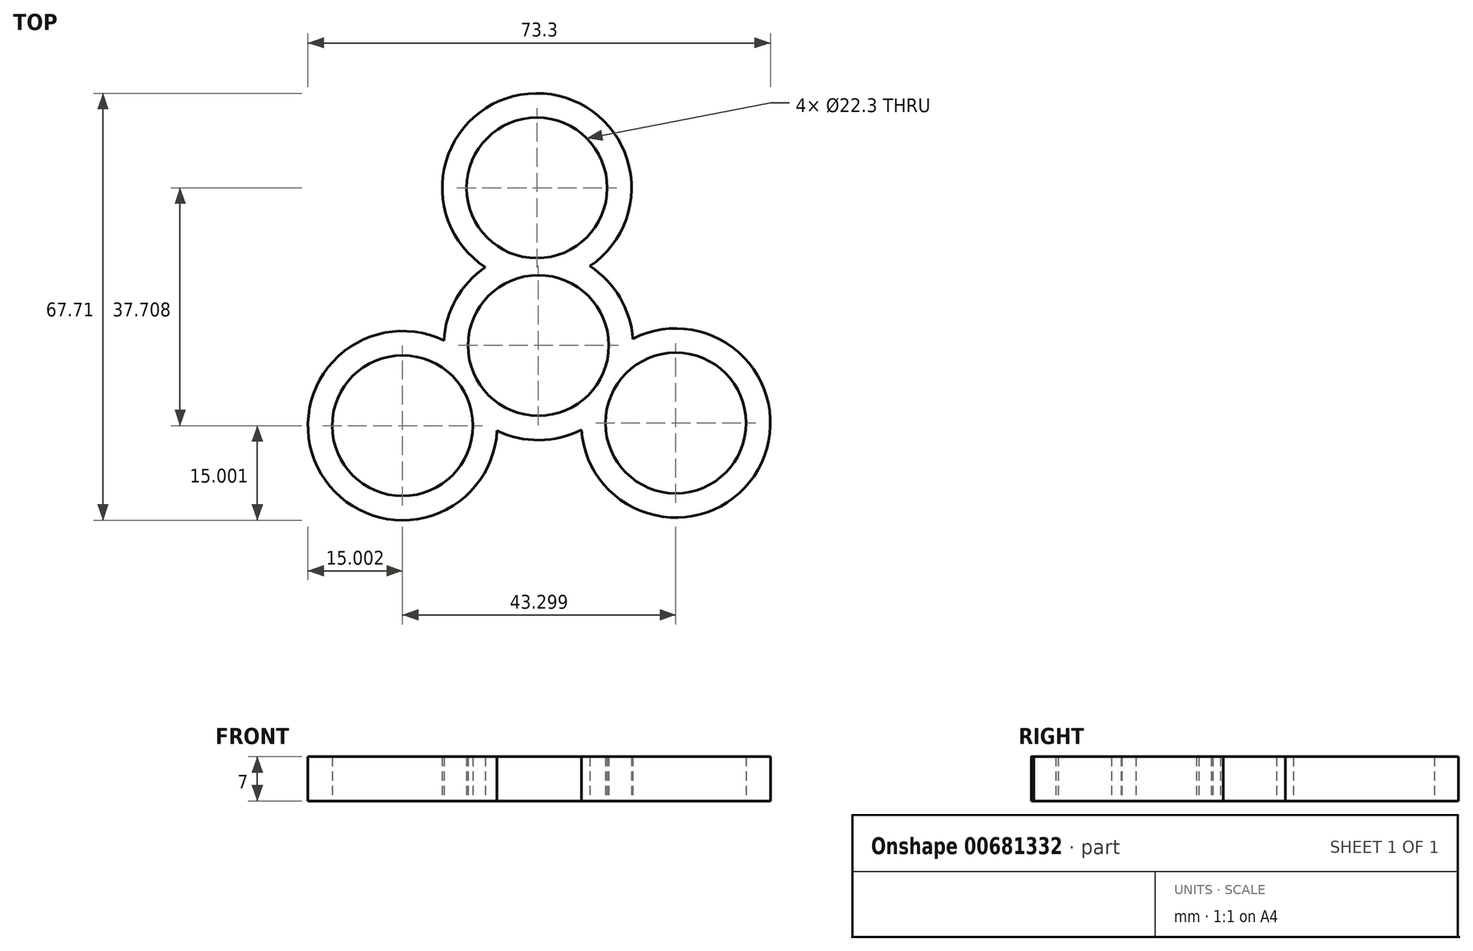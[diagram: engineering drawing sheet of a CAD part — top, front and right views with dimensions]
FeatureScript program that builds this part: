
annotation { "Feature Type Name" : "Feature", "Feature Type Description" : "" }
export const myFeature = defineFeature(function(context is Context, id is Id, definition is map)
    precondition{}
    {
        {
            var Q0;
            Q0=qCreatedBy(makeId("Top.planeOp"),FACE);
            var sketch = newSketch(context, id + "F0", { "sketchPlane" : qUnion([Q0])});
            skPoint(sketch, "E0.0.midPoint", {"position": v(22.1, 13.05) * mm});
            skLineSegment(sketch, "E1", {"start": v(0, 0) * mm, "end": v(-0.49, 50) * mm});
            skLineSegment(sketch, "E2", {"start": v(0, 0) * mm, "end": v(43.54, -24.58) * mm});
            skLineSegment(sketch, "E3", {"start": v(0, 0) * mm, "end": v(-43.06, -25.42) * mm});
            skCircle(sketch, "E4", {"center": v(-21.53, -12.7) * mm, "radius": 11.15 * mm});
            skCircle(sketch, "E5", {"center": v(21.77, -12.29) * mm, "radius": 11.15 * mm});
            skCircle(sketch, "E6", {"center": v(-0.24, 25) * mm, "radius": 11.15 * mm});
            skCircle(sketch, "E7", {"center": v(0, 0) * mm, "radius": 11.15 * mm});
            skPoint(sketch, "E8", {"position": v(31.48, -17.77) * mm});
            skCircle(sketch, "E9", {"center": v(-0.24, 25) * mm, "radius": 15 * mm});
            skCircle(sketch, "E10", {"center": v(21.77, -12.29) * mm, "radius": 15 * mm});
            skCircle(sketch, "E11", {"center": v(-21.53, -12.7) * mm, "radius": 15 * mm});
            skCircle(sketch, "E12", {"center": v(0, 0) * mm, "radius": 15 * mm});
            skSolve(sketch);
        }
        {
            var Q0;
            {var subQ3=sQuery(id+"F0.wireOp",EDGE,"E1");var subQ5=sQuery(id+"F0.wireOp",EDGE,"E7");var subQ11=makeQuery(id+"F0.imprint","INTERSECT",VERTEX,{"derivedFrom":[subQ3,subQ5]});Q0=makeQuery(id+"F0.imprint","IMPRINT",FACE,{"disambiguationData":[TD([[makeQuery(id+"F0.imprint","IMPRINT",EDGE,{"disambiguationData":[TD([[subQ11,-1.0]])],"derivedFrom":subQ3}),-1.0]])]});}
            var Q1;
            {var subQ3=sQuery(id+"F0.wireOp",EDGE,"E2");var subQ9=sQuery(id+"F0.wireOp",EDGE,"E7");var subQ11=makeQuery(id+"F0.imprint","INTERSECT",VERTEX,{"derivedFrom":[subQ3,subQ9]});Q1=makeQuery(id+"F0.imprint","IMPRINT",FACE,{"disambiguationData":[TD([[makeQuery(id+"F0.imprint","IMPRINT",EDGE,{"disambiguationData":[TD([[subQ11,-1.0]])],"derivedFrom":subQ3}),-1.0]])]});}
            var Q2;
            {var subQ5=sQuery(id+"F0.wireOp",EDGE,"E7");var subQ6=sQuery(id+"F0.wireOp",EDGE,"E1");var subQ7=makeQuery(id+"F0.imprint","INTERSECT",VERTEX,{"derivedFrom":[subQ6,subQ5]});Q2=makeQuery(id+"F0.imprint","IMPRINT",FACE,{"disambiguationData":[TD([[makeQuery(id+"F0.imprint","IMPRINT",EDGE,{"disambiguationData":[TD([[subQ7,-1.0]])],"derivedFrom":subQ6}),1.0]])]});}
            var Q3;
            {var subQ0=sQuery(id+"F0.wireOp",EDGE,"E9");var subQ1=sQuery(id+"F0.wireOp",EDGE,"E7");var subQ2=makeQuery(id+"F0.imprint","INTERSECT",VERTEX,{"disambiguationData":[OD(1.0)],"derivedFrom":[subQ1,subQ0]});Q3=makeQuery(id+"F0.imprint","IMPRINT",FACE,{"disambiguationData":[TD([[makeQuery(id+"F0.imprint","IMPRINT",EDGE,{"disambiguationData":[TD([[subQ2,-1.0]])],"derivedFrom":subQ1}),-1.0]])]});}
            var Q4;
            {var subQ0=sQuery(id+"F0.wireOp",EDGE,"E9");var subQ1=sQuery(id+"F0.wireOp",EDGE,"E7");var subQ2=makeQuery(id+"F0.imprint","INTERSECT",VERTEX,{"disambiguationData":[OD(0.0)],"derivedFrom":[subQ1,subQ0]});Q4=makeQuery(id+"F0.imprint","IMPRINT",FACE,{"disambiguationData":[TD([[makeQuery(id+"F0.imprint","IMPRINT",EDGE,{"disambiguationData":[TD([[subQ2,1.0]])],"derivedFrom":subQ1}),-1.0]])]});}
            var Q5;
            {var subQ0=sQuery(id+"F0.wireOp",EDGE,"E11");var subQ1=sQuery(id+"F0.wireOp",EDGE,"E7");var subQ2=makeQuery(id+"F0.imprint","INTERSECT",VERTEX,{"disambiguationData":[OD(1.0)],"derivedFrom":[subQ1,subQ0]});Q5=makeQuery(id+"F0.imprint","IMPRINT",FACE,{"disambiguationData":[TD([[makeQuery(id+"F0.imprint","IMPRINT",EDGE,{"disambiguationData":[TD([[subQ2,-1.0]])],"derivedFrom":subQ1}),-1.0]])]});}
            var Q6;
            {var subQ5=sQuery(id+"F0.wireOp",EDGE,"E7");var subQ6=sQuery(id+"F0.wireOp",EDGE,"E2");var subQ7=makeQuery(id+"F0.imprint","INTERSECT",VERTEX,{"derivedFrom":[subQ6,subQ5]});Q6=makeQuery(id+"F0.imprint","IMPRINT",FACE,{"disambiguationData":[TD([[makeQuery(id+"F0.imprint","IMPRINT",EDGE,{"disambiguationData":[TD([[subQ7,-1.0]])],"derivedFrom":subQ6}),1.0]])]});}
            var Q7;
            {var subQ5=sQuery(id+"F0.wireOp",EDGE,"E7");var subQ6=sQuery(id+"F0.wireOp",EDGE,"E3");var subQ7=makeQuery(id+"F0.imprint","INTERSECT",VERTEX,{"derivedFrom":[subQ6,subQ5]});Q7=makeQuery(id+"F0.imprint","IMPRINT",FACE,{"disambiguationData":[TD([[makeQuery(id+"F0.imprint","IMPRINT",EDGE,{"disambiguationData":[TD([[subQ7,-1.0]])],"derivedFrom":subQ6}),-1.0]])]});}
            var Q8;
            {var subQ5=sQuery(id+"F0.wireOp",EDGE,"E3");var subQ7=sQuery(id+"F0.wireOp",EDGE,"E7");var subQ8=makeQuery(id+"F0.imprint","INTERSECT",VERTEX,{"derivedFrom":[subQ5,subQ7]});Q8=makeQuery(id+"F0.imprint","IMPRINT",FACE,{"disambiguationData":[TD([[makeQuery(id+"F0.imprint","IMPRINT",EDGE,{"disambiguationData":[TD([[subQ8,-1.0]])],"derivedFrom":subQ5}),1.0]])]});}
            var Q9;
            {var subQ0=sQuery(id+"F0.wireOp",EDGE,"E11");var subQ1=sQuery(id+"F0.wireOp",EDGE,"E3");var subQ2=makeQuery(id+"F0.imprint","INTERSECT",VERTEX,{"disambiguationData":[OD(0.0)],"derivedFrom":[subQ1,subQ0]});Q9=makeQuery(id+"F0.imprint","IMPRINT",FACE,{"disambiguationData":[TD([[makeQuery(id+"F0.imprint","IMPRINT",EDGE,{"disambiguationData":[TD([[subQ2,1.0]])],"derivedFrom":subQ1}),1.0]])]});}
            var Q10;
            {var subQ0=sQuery(id+"F0.wireOp",EDGE,"E11");var subQ1=sQuery(id+"F0.wireOp",EDGE,"E3");var subQ2=makeQuery(id+"F0.imprint","INTERSECT",VERTEX,{"disambiguationData":[OD(0.0)],"derivedFrom":[subQ1,subQ0]});Q10=makeQuery(id+"F0.imprint","IMPRINT",FACE,{"disambiguationData":[TD([[makeQuery(id+"F0.imprint","IMPRINT",EDGE,{"disambiguationData":[TD([[subQ2,1.0]])],"derivedFrom":subQ1}),-1.0]])]});}
            var Q11;
            {var subQ0=sQuery(id+"F0.wireOp",EDGE,"E9");var subQ1=sQuery(id+"F0.wireOp",EDGE,"E1");var subQ2=makeQuery(id+"F0.imprint","INTERSECT",VERTEX,{"disambiguationData":[OD(0.0)],"derivedFrom":[subQ1,subQ0]});Q11=makeQuery(id+"F0.imprint","IMPRINT",FACE,{"disambiguationData":[TD([[makeQuery(id+"F0.imprint","IMPRINT",EDGE,{"disambiguationData":[TD([[subQ2,1.0]])],"derivedFrom":subQ1}),1.0]])]});}
            var Q12;
            {var subQ0=sQuery(id+"F0.wireOp",EDGE,"E9");var subQ1=sQuery(id+"F0.wireOp",EDGE,"E1");var subQ2=makeQuery(id+"F0.imprint","INTERSECT",VERTEX,{"disambiguationData":[OD(0.0)],"derivedFrom":[subQ1,subQ0]});Q12=makeQuery(id+"F0.imprint","IMPRINT",FACE,{"disambiguationData":[TD([[makeQuery(id+"F0.imprint","IMPRINT",EDGE,{"disambiguationData":[TD([[subQ2,1.0]])],"derivedFrom":subQ1}),-1.0]])]});}
            var Q13;
            {var subQ0=sQuery(id+"F0.wireOp",EDGE,"E10");var subQ1=sQuery(id+"F0.wireOp",EDGE,"E2");var subQ2=makeQuery(id+"F0.imprint","INTERSECT",VERTEX,{"disambiguationData":[OD(0.0)],"derivedFrom":[subQ1,subQ0]});Q13=makeQuery(id+"F0.imprint","IMPRINT",FACE,{"disambiguationData":[TD([[makeQuery(id+"F0.imprint","IMPRINT",EDGE,{"disambiguationData":[TD([[subQ2,1.0]])],"derivedFrom":subQ1}),1.0]])]});}
            var Q14;
            {var subQ0=sQuery(id+"F0.wireOp",EDGE,"E10");var subQ1=sQuery(id+"F0.wireOp",EDGE,"E2");var subQ2=makeQuery(id+"F0.imprint","INTERSECT",VERTEX,{"disambiguationData":[OD(0.0)],"derivedFrom":[subQ1,subQ0]});Q14=makeQuery(id+"F0.imprint","IMPRINT",FACE,{"disambiguationData":[TD([[makeQuery(id+"F0.imprint","IMPRINT",EDGE,{"disambiguationData":[TD([[subQ2,1.0]])],"derivedFrom":subQ1}),-1.0]])]});}
            extrude(context, id + "F1", {"entities" : qUnion([Q0, Q1, Q2, Q3, Q4, Q5, Q6, Q7, Q8, Q9, Q10, Q11, Q12, Q13, Q14]), "depth" : 7 * mm, "offsetDistance" : 25 * mm});
        }
    });
